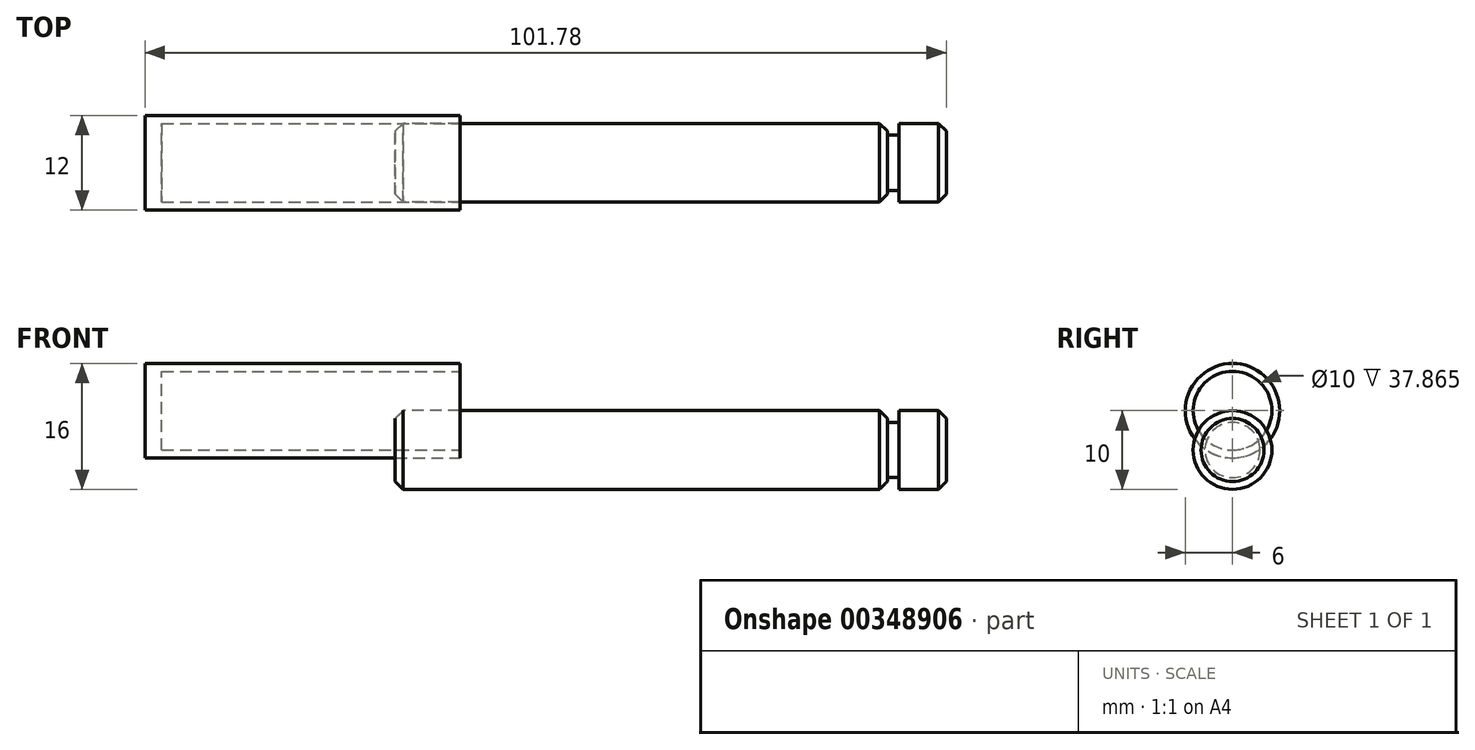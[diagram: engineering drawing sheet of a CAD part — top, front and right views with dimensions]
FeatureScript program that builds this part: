
annotation { "Feature Type Name" : "Feature", "Feature Type Description" : "" }
export const myFeature = defineFeature(function(context is Context, id is Id, definition is map)
    precondition{}
    {
        {
            var Q0;
            Q0=qCreatedBy(makeId("Front.planeOp"),FACE);
            var sketch = newSketch(context, id + "F0", { "sketchPlane" : qUnion([Q0])});
            skLineSegment(sketch, "E0", {"start": v(-83.15, 0) * mm, "end": v(-13.15, 0) * mm});
            skLineSegment(sketch, "E1.0", {"start": v(-83.15, 5) * mm, "end": v(-20.65, 5) * mm});
            skLineSegment(sketch, "E2", {"start": v(-13.15, 5) * mm, "end": v(-13.15, 0) * mm});
            skLineSegment(sketch, "E3.0", {"start": v(-19.15, 5) * mm, "end": v(-19.15, 3.5) * mm});
            skLineSegment(sketch, "E4", {"start": v(-83.15, 0) * mm, "end": v(-83.15, 5) * mm});
            skLineSegment(sketch, "E5.0", {"start": v(-20.65, 5) * mm, "end": v(-20.65, 3.5) * mm});
            skLineSegment(sketch, "E6.trimOffspring", {"start": v(-20.65, 3.5) * mm, "end": v(-19.15, 3.5) * mm});
            skLineSegment(sketch, "E7.trimOffspring", {"start": v(-19.15, 5) * mm, "end": v(-13.15, 5) * mm});
            skLineSegment(sketch, "E8.bottom", {"start": v(-74.93, 0) * mm, "end": v(-112.8, 0) * mm});
            skLineSegment(sketch, "E8.top", {"start": v(-74.93, 5) * mm, "end": v(-114.93, 5) * mm});
            skLineSegment(sketch, "E9.top", {"start": v(-74.93, -1) * mm, "end": v(-114.93, -1) * mm});
            skLineSegment(sketch, "E9.left", {"start": v(-74.93, 0) * mm, "end": v(-74.93, -1) * mm});
            skLineSegment(sketch, "E9.right", {"start": v(-114.93, 0) * mm, "end": v(-114.93, -1) * mm});
            skLineSegment(sketch, "E10", {"start": v(-114.93, 0) * mm, "end": v(-114.93, 5) * mm});
            skLineSegment(sketch, "E11", {"start": v(-112.8, -1) * mm, "end": v(-112.8, 5) * mm});
            skSolve(sketch);
        }
        {
            var Q0;
            {var subQ1=sQuery(id+"F0.wireOp",EDGE,"E0");Q0=makeQuery(id+"F0.imprint","IMPRINT",FACE,{"disambiguationData":[TD([[makeQuery(id+"F0.imprint","IMPRINT",EDGE,{"derivedFrom":subQ1}),1.0]])]});}
            var Q1;
            Q1=sQuery(id+"F0.wireOp",EDGE,"E0");
            revolve(context, id + "F1", {"entities" : qUnion([Q0]), "axis" : qUnion([Q1]), "revolveType" : RevolveType.FULL});
        }
        {
            var Q0;
            Q0=makeQuery(id+"F1.opRevolve","SWEPT_EDGE",EDGE,{"disambiguationData":[OSD([sQuery(id+"F0.wireOp",EDGE,"a03fbee8-2e0a-4c8b-9d5f-491997530557.0"),sQuery(id+"F0.wireOp",EDGE,"E4")])]});
            var Q1;
            Q1=makeQuery(id+"F1.opRevolve","SWEPT_EDGE",EDGE,{"disambiguationData":[OSD([sQuery(id+"F0.wireOp",EDGE,"E1.0"),sQuery(id+"F0.wireOp",EDGE,"828546c2-3b29-4b0d-96e1-b25bbb1505cc.0")])]});
            var Q2;
            Q2=makeQuery(id+"F1.opRevolve","SWEPT_EDGE",EDGE,{"disambiguationData":[OSD([sQuery(id+"F0.wireOp",EDGE,"E2"),sQuery(id+"F0.wireOp",EDGE,"E7.trimOffspring")])]});
            var Q3;
            Q3=makeQuery(id+"F1.opRevolve","SWEPT_EDGE",EDGE,{"disambiguationData":[OSD([sQuery(id+"F0.wireOp",EDGE,"E1.0"),sQuery(id+"F0.wireOp",EDGE,"E5.0")])]});
            chamfer(context, id + "F2", {"entities" : qUnion([Q0, Q1, Q2, Q3]), "width" : 1 * mm, "tangentPropagation" : true});
        }
        {
            var Q0;
            Q0=makeQuery(id+"F0.imprint","IMPRINT",FACE,{"disambiguationData":[TD([[makeQuery(id+"F0.imprint","IMPRINT",EDGE,{"derivedFrom":sQuery(id+"F0.wireOp",EDGE,"E9.top")}),-1.0]])]});
            var Q1;
            {var subQ0=sQuery(id+"F0.wireOp",EDGE,"E9.right");Q1=makeQuery(id+"F0.imprint","IMPRINT",FACE,{"disambiguationData":[TD([[makeQuery(id+"F0.imprint","IMPRINT",EDGE,{"derivedFrom":subQ0}),1.0]])]});}
            var Q2;
            Q2=sQuery(id+"F0.wireOp",EDGE,"E8.top");
            revolve(context, id + "F3", {"entities" : qUnion([Q0, Q1]), "axis" : qUnion([Q2]), "revolveType" : RevolveType.FULL});
        }
    });
